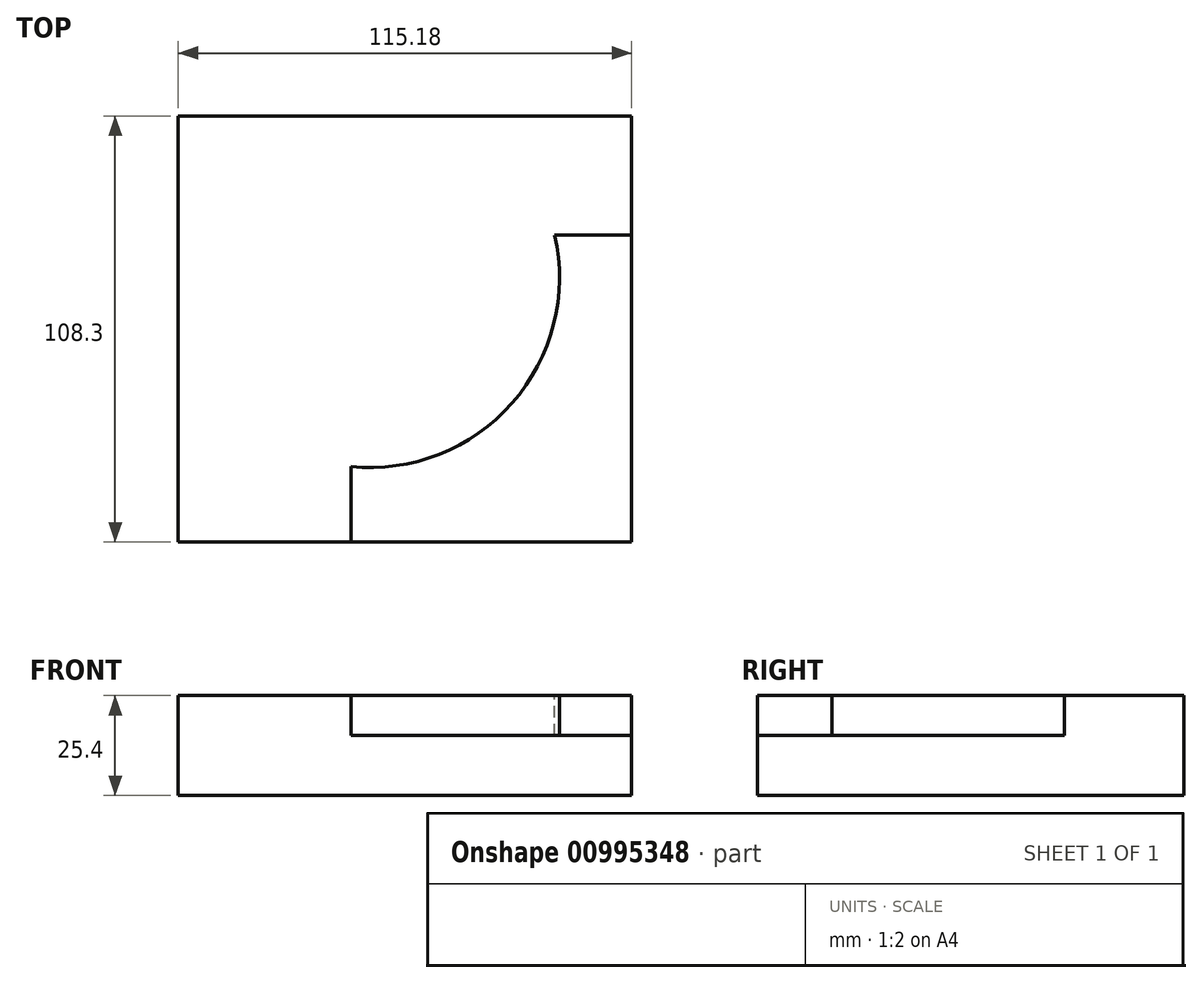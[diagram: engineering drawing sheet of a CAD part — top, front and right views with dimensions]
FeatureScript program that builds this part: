
annotation { "Feature Type Name" : "Feature", "Feature Type Description" : "" }
export const myFeature = defineFeature(function(context is Context, id is Id, definition is map)
    precondition{}
    {
        {
            var Q0;
            Q0=qCreatedBy(makeId("Top.planeOp"),FACE);
            var sketch = newSketch(context, id + "F0", { "sketchPlane" : qUnion([Q0])});
            skLineSegment(sketch, "E0.bottom", {"start": v(-57.6, -54.15) * mm, "end": v(57.6, -54.15) * mm});
            skLineSegment(sketch, "E0.top", {"start": v(-57.6, 54.15) * mm, "end": v(57.6, 54.15) * mm});
            skLineSegment(sketch, "E0.left", {"start": v(-57.6, -54.15) * mm, "end": v(-57.6, 54.15) * mm});
            skLineSegment(sketch, "E0.right", {"start": v(57.6, -54.15) * mm, "end": v(57.6, 54.15) * mm});
            skPoint(sketch, "E0.middle", {"position": v(0, 0) * mm});
            skLineSegment(sketch, "E1", {"start": v(-27.47, -54.15) * mm, "end": v(-27.47, -16.17) * mm});
            skLineSegment(sketch, "E2", {"start": v(57.6, 37.56) * mm, "end": v(15.4, 37.56) * mm});
            skArc(sketch, "E3", {"start": v(-27.47, -16.17) * mm, "mid": v(18, -8.48) * mm, "end": v(15.4, 37.56) * mm});
            skLineSegment(sketch, "E4.0", {"start": v(57.6, 23.85) * mm, "end": v(38.04, 23.85) * mm});
            skArc(sketch, "E4.1", {"start": v(-13.76, -34.97) * mm, "mid": v(27.2, -18.83) * mm, "end": v(38.04, 23.85) * mm});
            skLineSegment(sketch, "E4.2", {"start": v(-13.76, -54.15) * mm, "end": v(-13.76, -34.97) * mm});
            skSolve(sketch);
        }
        {
            var Q0;
            {var subQ1=sQuery(id+"F0.wireOp",EDGE,"E1");Q0=makeQuery(id+"F0.imprint","IMPRINT",FACE,{"disambiguationData":[TD([[makeQuery(id+"F0.imprint","IMPRINT",EDGE,{"derivedFrom":subQ1}),-1.0]])]});}
            var Q1;
            {var subQ0=sQuery(id+"F0.wireOp",EDGE,"E4.0");Q1=makeQuery(id+"F0.imprint","IMPRINT",FACE,{"disambiguationData":[TD([[makeQuery(id+"F0.imprint","IMPRINT",EDGE,{"derivedFrom":subQ0}),1.0]])]});}
            var Q2;
            {var subQ1=sQuery(id+"F0.wireOp",EDGE,"E0.top");Q2=makeQuery(id+"F0.imprint","IMPRINT",FACE,{"disambiguationData":[TD([[makeQuery(id+"F0.imprint","IMPRINT",EDGE,{"derivedFrom":subQ1}),-1.0]])]});}
            extrude(context, id + "F1", {"entities" : qUnion([Q0, Q1, Q2]), "depth" : 25.4 * mm, "offsetDistance" : 25.4 * mm});
        }
        {
            var Q0;
            Q0=makeQuery(id+"F1.opExtrude","CAP_FACE",FACE,{"disambiguationData":[OSD([sQuery(id+"F0.wireOp",EDGE,"E0.bottom"),sQuery(id+"F0.wireOp",EDGE,"E0.top"),sQuery(id+"F0.wireOp",EDGE,"E0.left"),sQuery(id+"F0.wireOp",EDGE,"E0.right")])],"isStart":false});
            var sketch = newSketch(context, id + "F2", { "sketchPlane" : qUnion([Q0])});
            skArc(sketch, "E5.0", {"start": v(-13.76, -34.97) * mm, "mid": v(27.2, -18.83) * mm, "end": v(38.04, 23.85) * mm});
            skLineSegment(sketch, "E6.0", {"start": v(-13.76, -54.15) * mm, "end": v(-13.76, -34.97) * mm});
            skLineSegment(sketch, "E7.0", {"start": v(57.6, 23.85) * mm, "end": v(38.04, 23.85) * mm});
            skSolve(sketch);
        }
        {
            var Q0;
            Q0=makeQuery(id+"F2.imprint","IMPRINT",FACE,{"disambiguationData":[TD([[makeQuery(id+"F2.imprint","IMPRINT",EDGE,{"derivedFrom":sQuery(id+"F2.wireOp",EDGE,"E5.0")}),-1.0]])]});
            extrude(context, id + "F3", {"entities" : qUnion([Q0]), "operationType" : NewBodyOperationType.REMOVE, "oppositeDirection" : true, "depth" : 10.16 * mm, "offsetDistance" : 25.4 * mm});
        }
    });
